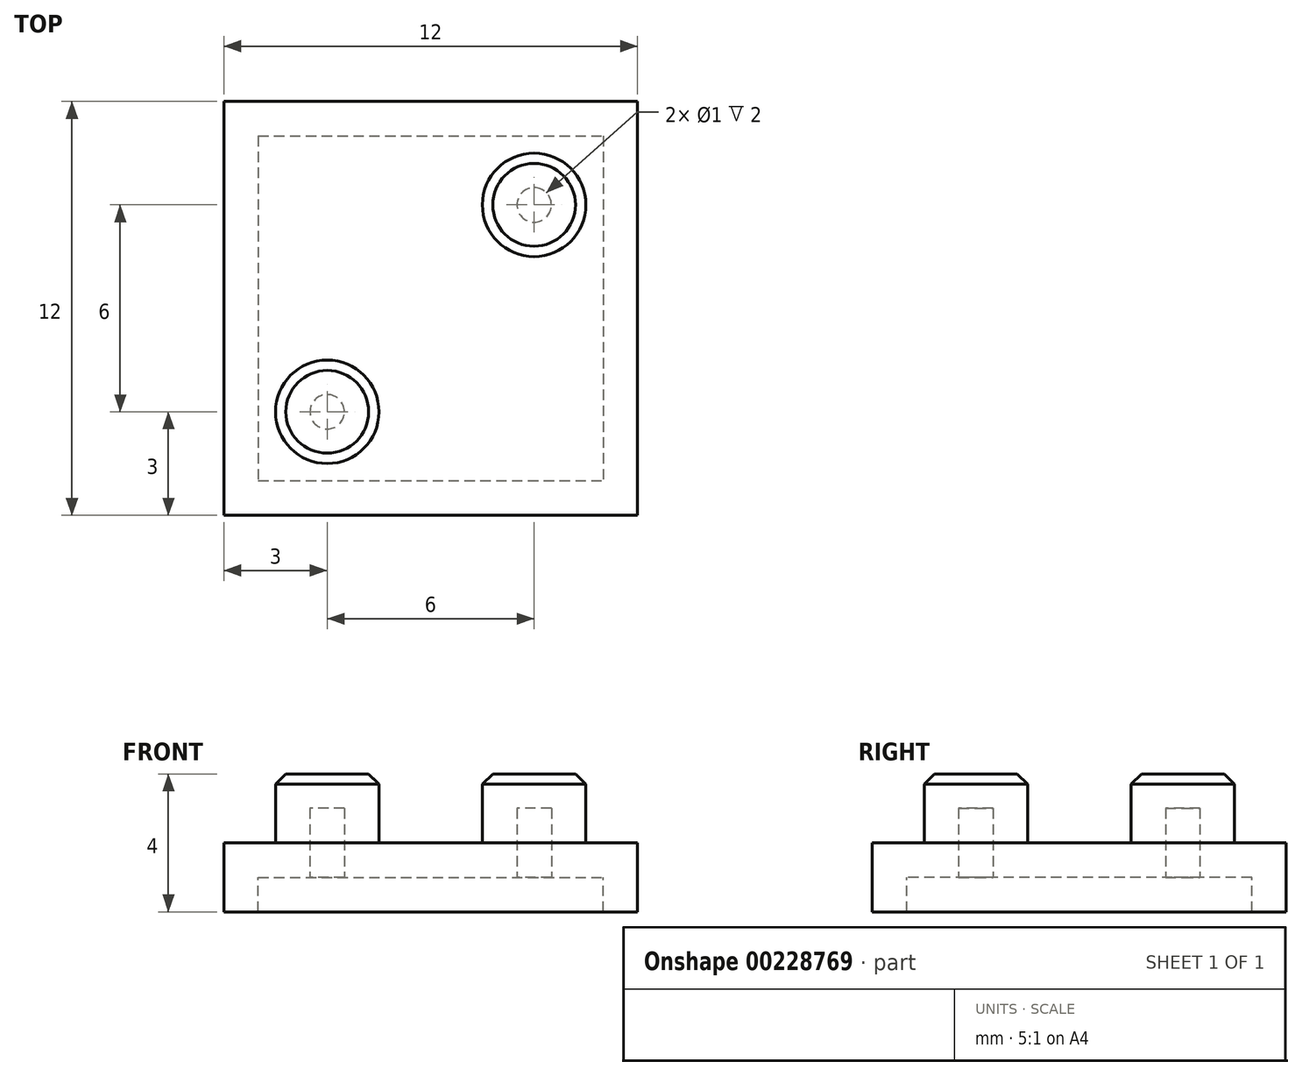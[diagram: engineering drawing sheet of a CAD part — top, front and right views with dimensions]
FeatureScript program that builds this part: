
annotation { "Feature Type Name" : "Feature", "Feature Type Description" : "" }
export const myFeature = defineFeature(function(context is Context, id is Id, definition is map)
    precondition{}
    {
        {
            var Q0;
            Q0=qCreatedBy(makeId("Top.planeOp"),FACE);
            var sketch = newSketch(context, id + "F3", { "sketchPlane" : qUnion([Q0])});
            skLineSegment(sketch, "E0.bottom", {"start": v(-6, 6) * mm, "end": v(6, 6) * mm});
            skLineSegment(sketch, "E0.top", {"start": v(-6, -6) * mm, "end": v(6, -6) * mm});
            skLineSegment(sketch, "E0.left", {"start": v(-6, 6) * mm, "end": v(-6, -6) * mm});
            skLineSegment(sketch, "E0.right", {"start": v(6, 6) * mm, "end": v(6, -6) * mm});
            skSolve(sketch);
        }
        {
            var Q0;
            Q0=makeQuery(id+"F3.imprint","IMPRINT",FACE,{"disambiguationData":[TD([[makeQuery(id+"F3.imprint","IMPRINT",EDGE,{"derivedFrom":sQuery(id+"F3.wireOp",EDGE,"E0.bottom")}),-1.0]])]});
            extrude(context, id + "F0", {"entities" : qUnion([Q0]), "oppositeDirection" : true, "depth" : 2 * mm});
        }
        {
            var Q0;
            Q0=qCreatedBy(makeId("Top.planeOp"),FACE);
            var sketch = newSketch(context, id + "F1", { "sketchPlane" : qUnion([Q0])});
            skCircle(sketch, "E1", {"center": v(3, 3) * mm, "radius": 1.5 * mm});
            skLineSegment(sketch, "E2", {"start": v(0, 3) * mm, "end": v(0, -3) * mm, "construction": true});
            skPoint(sketch, "E3.orphan", {"position": v(6, -6) * mm});
            skPoint(sketch, "E4.0.start.orphan", {"position": v(-6, -6) * mm});
            skCircle(sketch, "E5.MirrorC", {"center": v(-3, 3) * mm, "radius": 1.5 * mm});
            skLineSegment(sketch, "E6", {"start": v(-4.43, 0) * mm, "end": v(4.86, 0) * mm, "construction": true});
            skCircle(sketch, "E7.MirrorC", {"center": v(-3, -3) * mm, "radius": 1.5 * mm});
            skCircle(sketch, "E8.MirrorC", {"center": v(3, -3) * mm, "radius": 1.5 * mm});
            skSolve(sketch);
        }
        {
            var Q0;
            Q0=makeQuery(id+"F1.imprint","IMPRINT",FACE,{"disambiguationData":[TD([[makeQuery(id+"F1.imprint","IMPRINT",EDGE,{"derivedFrom":sQuery(id+"F1.wireOp",EDGE,"E1")}),1.0]])]});
            var Q1;
            Q1=makeQuery(id+"F1.imprint","IMPRINT",FACE,{"disambiguationData":[TD([[makeQuery(id+"F1.imprint","IMPRINT",EDGE,{"derivedFrom":sQuery(id+"F1.wireOp",EDGE,"E5.MirrorC")}),-1.0]])]});
            var Q2;
            Q2=makeQuery(id+"F1.imprint","IMPRINT",FACE,{"disambiguationData":[TD([[makeQuery(id+"F1.imprint","IMPRINT",EDGE,{"derivedFrom":sQuery(id+"F1.wireOp",EDGE,"E8.MirrorC")}),-1.0]])]});
            var Q3;
            Q3=makeQuery(id+"F1.imprint","IMPRINT",FACE,{"disambiguationData":[TD([[makeQuery(id+"F1.imprint","IMPRINT",EDGE,{"derivedFrom":sQuery(id+"F1.wireOp",EDGE,"E7.MirrorC")}),1.0]])]});
            var Q4;
            Q4=sQuery(id+"F1.wireOp",EDGE,"E5.MirrorC");
            var Q5;
            Q5=sQuery(id+"F1.wireOp",EDGE,"E1");
            extrude(context, id + "F4", {"entities" : qUnion([Q0, Q1, Q2, Q3]), "operationType" : NewBodyOperationType.ADD, "surfaceEntities" : qUnion([Q4, Q5]), "depth" : 2 * mm});
        }
        {
            var Q0;
            Q0=makeQuery(id+"F4.opExtrude","CAP_EDGE",EDGE,{"disambiguationData":[OSD([sQuery(id+"F1.wireOp",EDGE,"E5.MirrorC")])],"isStart":false});
            var Q1;
            Q1=makeQuery(id+"F4.opExtrude","CAP_EDGE",EDGE,{"disambiguationData":[OSD([sQuery(id+"F1.wireOp",EDGE,"E1")])],"isStart":false});
            var Q2;
            Q2=makeQuery(id+"F4.opExtrude","CAP_EDGE",EDGE,{"disambiguationData":[OSD([sQuery(id+"F1.wireOp",EDGE,"E7.MirrorC")])],"isStart":false});
            var Q3;
            Q3=makeQuery(id+"F4.opExtrude","CAP_EDGE",EDGE,{"disambiguationData":[OSD([sQuery(id+"F1.wireOp",EDGE,"E8.MirrorC")])],"isStart":false});
            chamfer(context, id + "F5", {"entities" : qUnion([Q0, Q1, Q2, Q3]), "width" : 0.3 * mm, "tangentPropagation" : true});
        }
        {
            var Q0;
            Q0=makeQuery(id+"F0.opExtrude","CAP_FACE",FACE,{"disambiguationData":[OSD([sQuery(id+"F3.wireOp",EDGE,"E0.bottom"),sQuery(id+"F3.wireOp",EDGE,"E0.top"),sQuery(id+"F3.wireOp",EDGE,"E0.left"),sQuery(id+"F3.wireOp",EDGE,"E0.right")])],"isStart":false});
            shell(context, id + "F2", {"entities" : qUnion([Q0]), "thickness" : 1 * mm});
        }
    });
